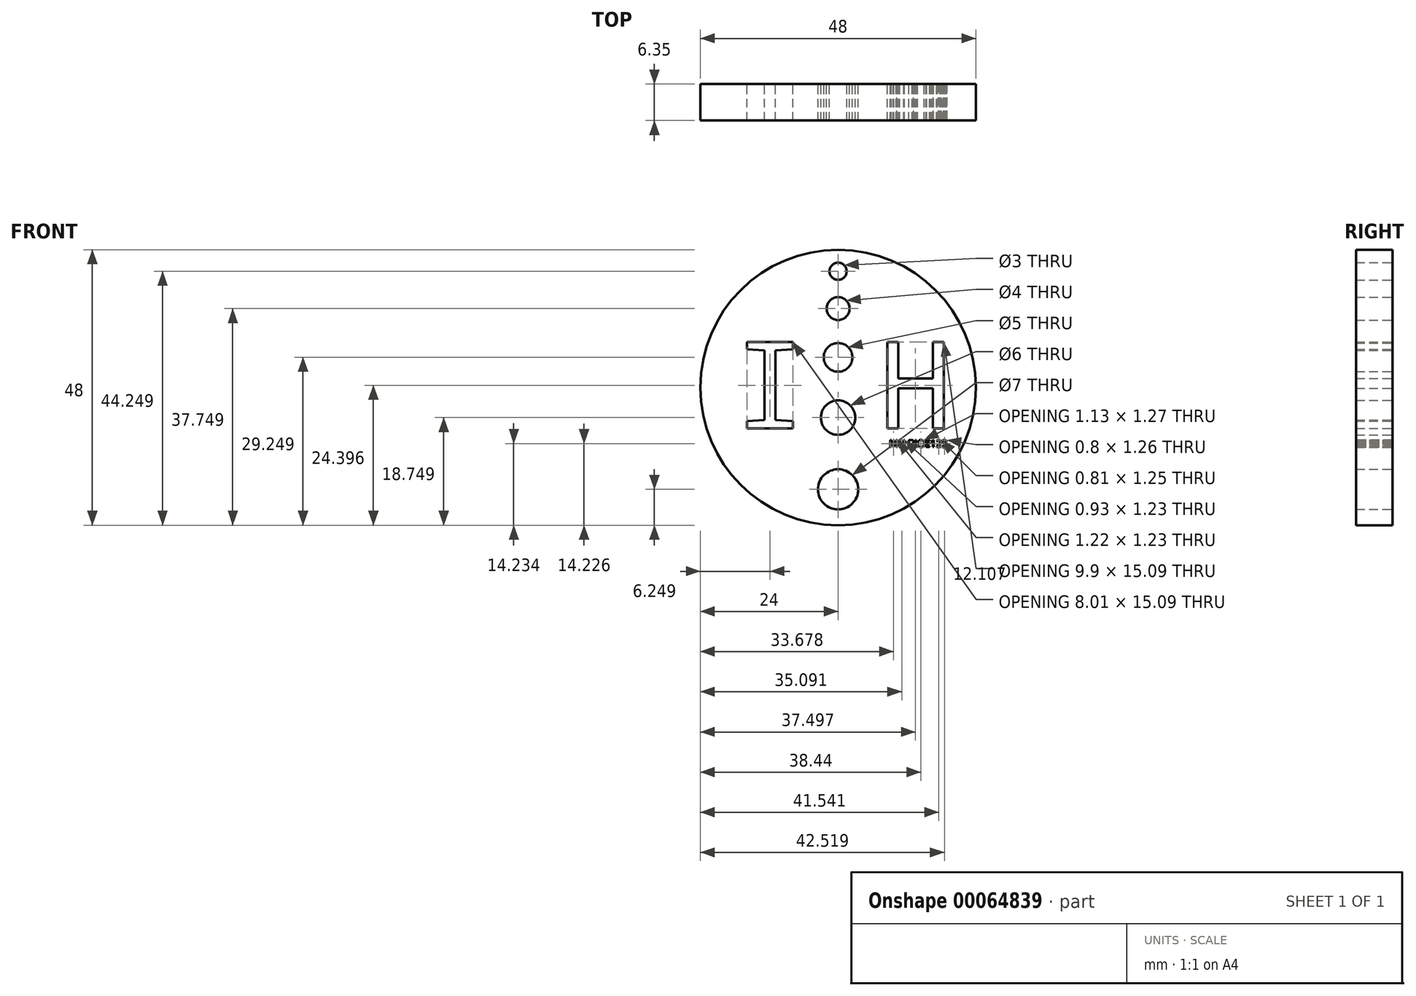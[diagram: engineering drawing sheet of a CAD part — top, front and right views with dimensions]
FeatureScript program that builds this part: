
annotation { "Feature Type Name" : "Feature", "Feature Type Description" : "" }
export const myFeature = defineFeature(function(context is Context, id is Id, definition is map)
    precondition{}
    {
        {
            var Q0;
            Q0=qCreatedBy(makeId("Front.planeOp"),FACE);
            var sketch = newSketch(context, id + "F0", { "sketchPlane" : qUnion([Q0])});
            skCircle(sketch, "E0", {"center": v(0, -2.32) * mm, "radius": 27.5 * mm});
            skCircle(sketch, "E1", {"center": v(0, -2.32) * mm, "radius": 24 * mm});
            skText(sketch, "E2", { "text": "I H", "fontName": "DroidSansMono.ttf"});
            skCircle(sketch, "E3", {"center": v(0, 17.93) * mm, "radius": 1.5 * mm});
            skCircle(sketch, "E4", {"center": v(0, 11.43) * mm, "radius": 2 * mm});
            skCircle(sketch, "E5", {"center": v(0, 2.93) * mm, "radius": 2.5 * mm});
            skCircle(sketch, "E6", {"center": v(0, -7.57) * mm, "radius": 3 * mm});
            skCircle(sketch, "E7", {"center": v(0, -20.07) * mm, "radius": 3.5 * mm});
            skText(sketch, "E8", { "text": "MH BIOE123", "fontName": "OpenSans-Regular.ttf"});
            const initialGuessF0  = {"E2": [-0.01822, -0.00947, 1, 0, 0.01522], "E8": [0.0089, -0.01271, 1, 0, 0.00124]};
            skSetInitialGuess(sketch, initialGuessF0);
            skSolve(sketch);
        }
        {
            var Q0;
            Q0=makeQuery(id+"F0.imprint","IMPRINT",FACE,{"disambiguationData":[TD([[makeQuery(id+"F0.imprint","IMPRINT",EDGE,{"derivedFrom":sQuery(id+"F0.wireOp",EDGE,"E1")}),1.0]])]});
            extrude(context, id + "F1", {"entities" : qUnion([Q0]), "depth" : 6.35 * mm});
        }
    });
